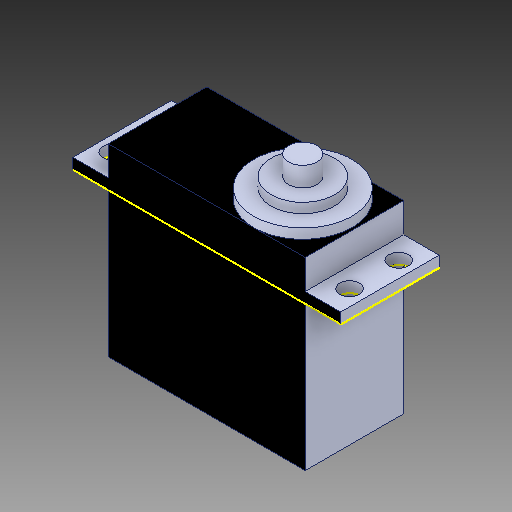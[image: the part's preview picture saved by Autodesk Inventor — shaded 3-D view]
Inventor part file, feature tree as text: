
AUTODESK INVENTOR PART (.ipt)
format: ipt  version: 2018 (Build 220112000, 112)  size: 166,912 bytes
history: native  units: mm
features: other x3, sketch x1
ambient origin geometry x8: Origin, YZ Plane, XZ Plane, XY Plane, X Axis, Y Axis, Z Axis, Center Point
bodies: Solid1 (feature_tree)
feature tree (4):
  other  "SERVOMG996R_MIR.ipt"
  other  "Solid1::SERVOMG996R_MIR.ipt"
  other  "TaggingFeature1"
  sketch  "Sketch7"  dims[d0=10.0mm]
